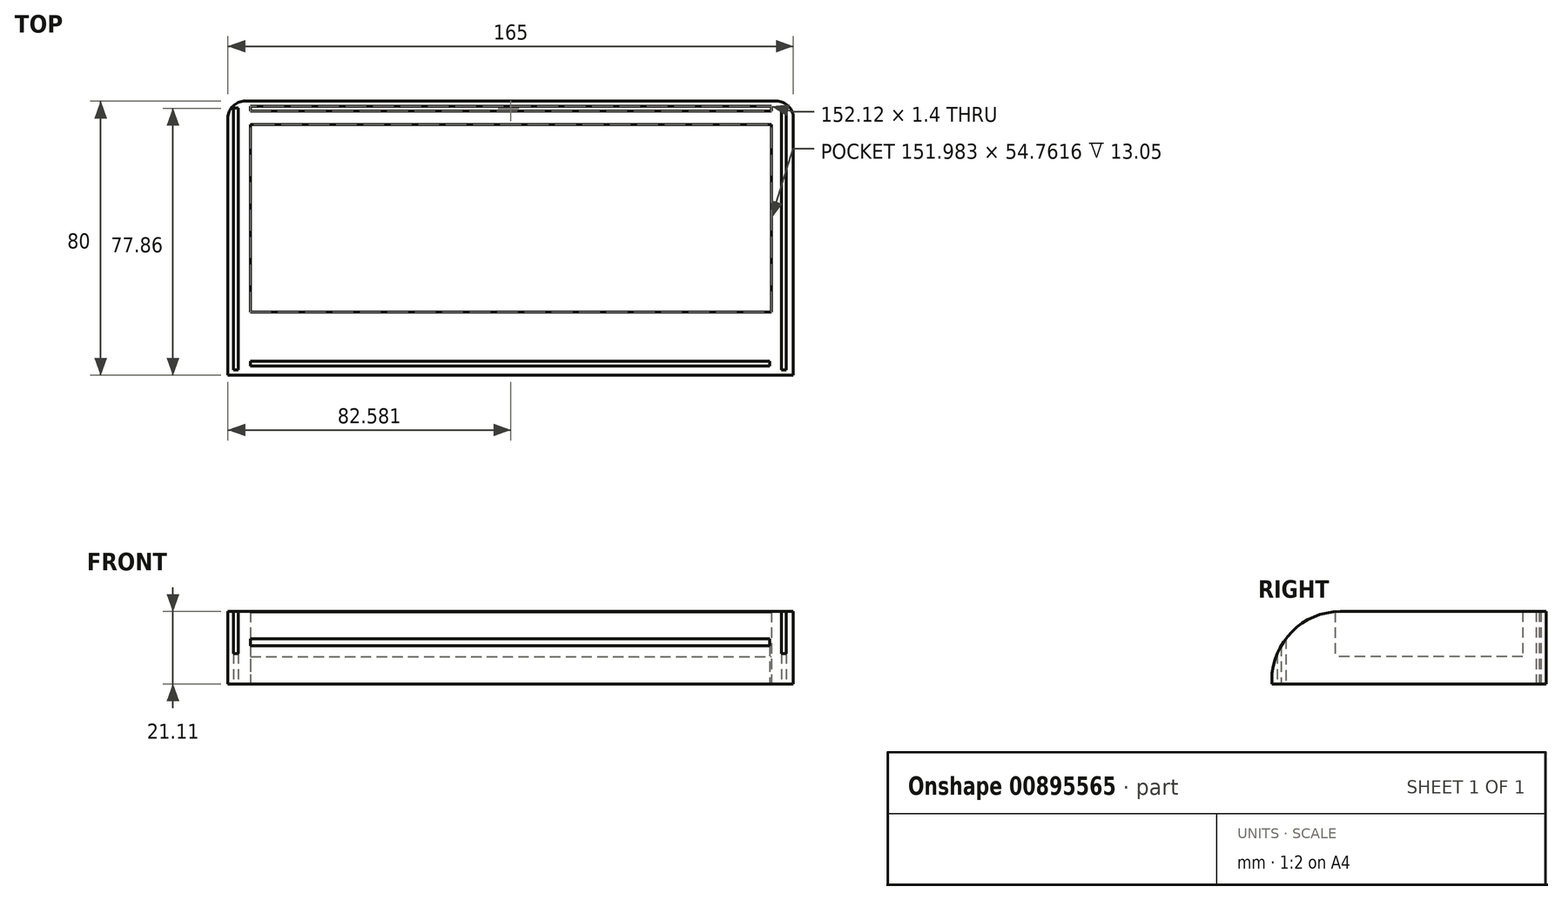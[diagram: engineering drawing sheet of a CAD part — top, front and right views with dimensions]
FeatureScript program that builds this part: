
annotation { "Feature Type Name" : "Feature", "Feature Type Description" : "" }
export const myFeature = defineFeature(function(context is Context, id is Id, definition is map)
    precondition{}
    {
        {
            var Q0;
            Q0=qCreatedBy(makeId("Top.planeOp"),FACE);
            var sketch = newSketch(context, id + "F0", { "sketchPlane" : qUnion([Q0])});
            skLineSegment(sketch, "E0.bottom", {"start": v(-83.02, 42.85) * mm, "end": v(81.98, 42.85) * mm});
            skLineSegment(sketch, "E0.top", {"start": v(-83.02, -37.15) * mm, "end": v(81.98, -37.15) * mm});
            skLineSegment(sketch, "E0.left", {"start": v(-83.02, 42.85) * mm, "end": v(-83.02, -37.15) * mm});
            skLineSegment(sketch, "E0.right", {"start": v(81.98, 42.85) * mm, "end": v(81.98, -37.15) * mm});
            skLineSegment(sketch, "E1.bottom", {"start": v(-83.02, 42.85) * mm, "end": v(-83.02, 42.85) * mm});
            skLineSegment(sketch, "E1.top", {"start": v(-83.02, -37.15) * mm, "end": v(-83.02, -37.15) * mm});
            skLineSegment(sketch, "E2.bottom", {"start": v(-76.43, 36.06) * mm, "end": v(75.55, 36.06) * mm});
            skLineSegment(sketch, "E2.top", {"start": v(-76.43, -18.7) * mm, "end": v(75.55, -18.7) * mm});
            skLineSegment(sketch, "E2.left", {"start": v(-76.43, 36.06) * mm, "end": v(-76.43, -18.7) * mm});
            skLineSegment(sketch, "E2.right", {"start": v(75.55, 36.06) * mm, "end": v(75.55, -18.7) * mm});
            skPoint(sketch, "E3", {"position": v(-0.52, 42.85) * mm});
            skLineSegment(sketch, "E4.bottom", {"start": v(-76.5, 41.4) * mm, "end": v(75.62, 41.4) * mm});
            skLineSegment(sketch, "E4.top", {"start": v(-76.5, 40) * mm, "end": v(75.62, 40) * mm});
            skLineSegment(sketch, "E4.left", {"start": v(-76.5, 41.4) * mm, "end": v(-76.5, 40) * mm});
            skLineSegment(sketch, "E4.right", {"start": v(75.62, 41.4) * mm, "end": v(75.62, 40) * mm});
            skLineSegment(sketch, "E5.bottom", {"start": v(-81.45, 40.85) * mm, "end": v(-80.05, 40.85) * mm});
            skLineSegment(sketch, "E5.top", {"start": v(-81.45, -35.57) * mm, "end": v(-80.05, -35.57) * mm});
            skLineSegment(sketch, "E5.left", {"start": v(-81.45, 40.85) * mm, "end": v(-81.45, -35.57) * mm});
            skLineSegment(sketch, "E5.right", {"start": v(-80.05, 40.85) * mm, "end": v(-80.05, -35.57) * mm});
            skLineSegment(sketch, "E6.bottom", {"start": v(-76.43, -33.07) * mm, "end": v(75.12, -33.07) * mm});
            skLineSegment(sketch, "E6.top", {"start": v(-76.43, -34.47) * mm, "end": v(75.12, -34.47) * mm});
            skLineSegment(sketch, "E6.left", {"start": v(-76.43, -33.07) * mm, "end": v(-76.43, -34.47) * mm});
            skLineSegment(sketch, "E6.right", {"start": v(75.12, -33.07) * mm, "end": v(75.12, -34.47) * mm});
            skLineSegment(sketch, "E7.bottom", {"start": v(78.53, 40.99) * mm, "end": v(79.93, 40.99) * mm});
            skLineSegment(sketch, "E7.top", {"start": v(78.53, -35.57) * mm, "end": v(79.93, -35.57) * mm});
            skLineSegment(sketch, "E7.left", {"start": v(78.53, 40.99) * mm, "end": v(78.53, -35.57) * mm});
            skLineSegment(sketch, "E7.right", {"start": v(79.93, 40.99) * mm, "end": v(79.93, -35.57) * mm});
            skSolve(sketch);
        }
        {
            var Q0;
            Q0=makeQuery(id+"F0.imprint","IMPRINT",FACE,{"disambiguationData":[TD([[makeQuery(id+"F0.imprint","IMPRINT",EDGE,{"derivedFrom":sQuery(id+"F0.wireOp",EDGE,"E0.bottom")}),-1.0]])]});
            extrude(context, id + "F1", {"entities" : qUnion([Q0]), "depth" : 21.1 * mm, "offsetDistance" : 25 * mm});
        }
        {
            var Q0;
            Q0=makeQuery(id+"F1.opExtrude","CAP_EDGE",EDGE,{"disambiguationData":[OSD([sQuery(id+"F0.wireOp",EDGE,"E0.top")])],"isStart":false});
            fillet(context, id + "F2", {"entities" : qUnion([Q0]), "radius" : 20 * mm, "tangentPropagation" : true, "allowEdgeOverflow" : false});
        }
        {
            var Q0;
            Q0=makeQuery(id+"F0.imprint","IMPRINT",FACE,{"disambiguationData":[TD([[makeQuery(id+"F0.imprint","IMPRINT",EDGE,{"derivedFrom":sQuery(id+"F0.wireOp",EDGE,"E2.bottom")}),-1.0]])]});
            extrude(context, id + "F3", {"entities" : qUnion([Q0]), "operationType" : NewBodyOperationType.ADD, "depth" : 8 * mm, "offsetDistance" : 25 * mm});
        }
        {
            var Q0;
            Q0=makeQuery(id+"F1.opExtrude","SWEPT_EDGE",EDGE,{"disambiguationData":[OSD([sQuery(id+"F0.wireOp",EDGE,"E0.bottom"),sQuery(id+"F0.wireOp",EDGE,"E0.left")])]});
            var Q1;
            Q1=makeQuery(id+"F1.opExtrude","SWEPT_EDGE",EDGE,{"disambiguationData":[OSD([sQuery(id+"F0.wireOp",EDGE,"E0.bottom"),sQuery(id+"F0.wireOp",EDGE,"E0.right")])]});
            fillet(context, id + "F4", {"entities" : qUnion([Q0, Q1]), "radius" : 5 * mm, "tangentPropagation" : true, "allowEdgeOverflow" : false});
        }
    });
